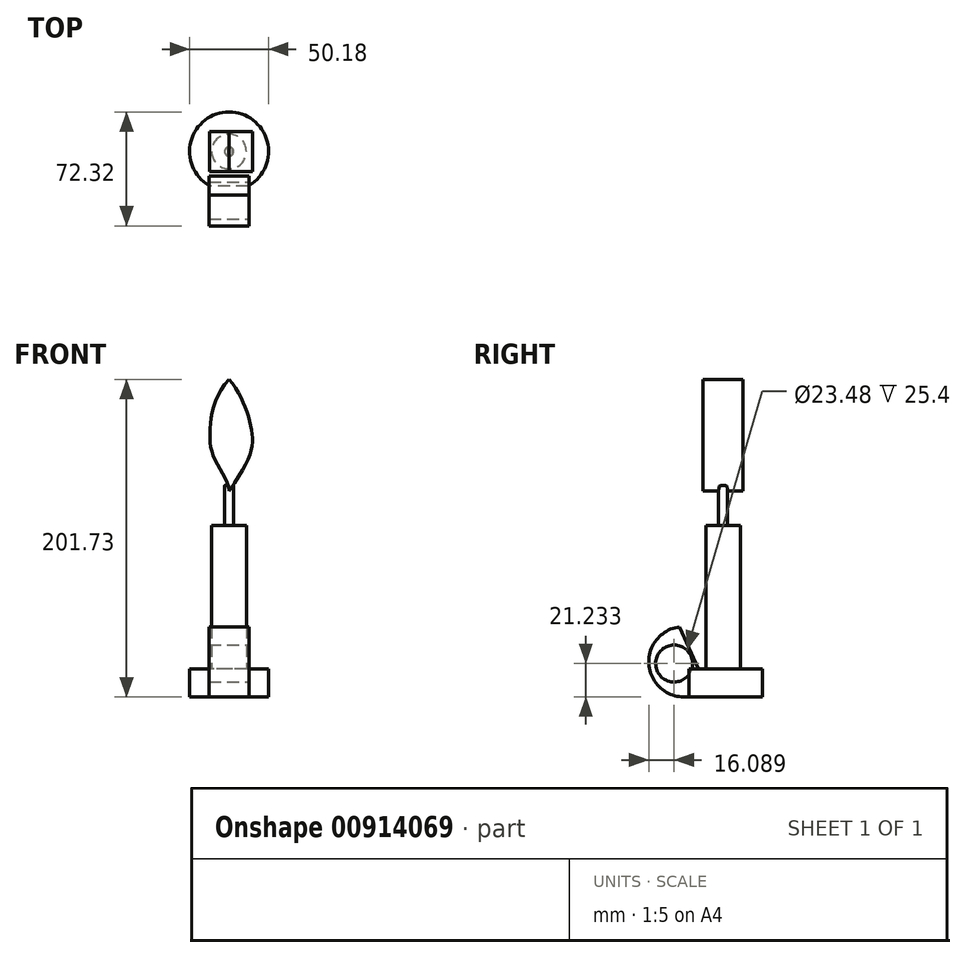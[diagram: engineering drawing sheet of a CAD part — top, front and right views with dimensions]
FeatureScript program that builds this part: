
annotation { "Feature Type Name" : "Feature", "Feature Type Description" : "" }
export const myFeature = defineFeature(function(context is Context, id is Id, definition is map)
    precondition{}
    {
        {
            var Q0;
            Q0=qCreatedBy(makeId("Top.planeOp"),FACE);
            var sketch = newSketch(context, id + "F0", { "sketchPlane" : qUnion([Q0])});
            skCircle(sketch, "E0", {"center": v(0, 0) * mm, "radius": 25.09 * mm});
            skCircle(sketch, "E1", {"center": v(0, 0) * mm, "radius": 9.92 * mm});
            skSolve(sketch);
        }
        {
            var Q0;
            Q0=makeQuery(id+"F0.imprint","IMPRINT",FACE,{"disambiguationData":[TD([[makeQuery(id+"F0.imprint","IMPRINT",EDGE,{"derivedFrom":sQuery(id+"F0.wireOp",EDGE,"E0")}),1.0]])]});
            extrude(context, id + "F1", {"entities" : qUnion([Q0]), "depth" : 17.53 * mm, "offsetDistance" : 25.4 * mm});
        }
        {
            var Q0;
            Q0=qCreatedBy(makeId("Top.planeOp"),FACE);
            var sketch = newSketch(context, id + "F2", { "sketchPlane" : qUnion([Q0])});
            skCircle(sketch, "E2", {"center": v(0, 0) * mm, "radius": 11.02 * mm});
            skSolve(sketch);
        }
        {
            var Q0;
            Q0=makeQuery(id+"F2.imprint","IMPRINT",FACE,{"disambiguationData":[TD([[makeQuery(id+"F2.imprint","IMPRINT",EDGE,{"derivedFrom":sQuery(id+"F2.wireOp",EDGE,"E2")}),1.0]])]});
            extrude(context, id + "F3", {"entities" : qUnion([Q0]), "operationType" : NewBodyOperationType.ADD, "depth" : 108.7 * mm, "offsetDistance" : 25.4 * mm});
        }
        {
            var Q0;
            Q0=makeQuery(id+"F3.opExtrude","CAP_FACE",FACE,{"disambiguationData":[OSD([sQuery(id+"F2.wireOp",EDGE,"E2")])],"isStart":false});
            cPlane(context, id + "F4", {"entities" : qUnion([Q0]), "cplaneType" : CPlaneType.OFFSET, "offset" : 25.4 * mm, "width" : 152.4 * mm, "height" : 152.4 * mm});
        }
        {
            var Q0;
            Q0=qCreatedBy(id+"F4.planeOp",FACE);
            var sketch = newSketch(context, id + "F5", { "sketchPlane" : qUnion([Q0])});
            skCircle(sketch, "E3", {"center": v(0, 0) * mm, "radius": 2.87 * mm});
            skSolve(sketch);
        }
        {
            var Q0;
            Q0=makeQuery(id+"F5.imprint","IMPRINT",FACE,{"disambiguationData":[TD([[makeQuery(id+"F5.imprint","IMPRINT",EDGE,{"derivedFrom":sQuery(id+"F5.wireOp",EDGE,"E3")}),1.0]])]});
            extrude(context, id + "F6", {"entities" : qUnion([Q0]), "operationType" : NewBodyOperationType.ADD, "oppositeDirection" : true, "depth" : 25.4 * mm, "offsetDistance" : 25.4 * mm});
        }
        {
            var Q0;
            Q0=qCreatedBy(makeId("Right.planeOp"),FACE);
            var sketch = newSketch(context, id + "F7", { "sketchPlane" : qUnion([Q0])});
            skArc(sketch, "E4", {"start": v(-27.61, 44.34) * mm, "mid": v(-47.05, 19.36) * mm, "end": v(-22.01, 0) * mm});
            skLineSegment(sketch, "E5", {"start": v(-27.61, 44.34) * mm, "end": v(-14, 13.6) * mm});
            skLineSegment(sketch, "E6", {"start": v(-14, 13.6) * mm, "end": v(-22.01, 0) * mm});
            skSolve(sketch);
        }
        {
            var Q0;
            Q0=makeQuery(id+"F7.imprint","IMPRINT",FACE,{"disambiguationData":[TD([[makeQuery(id+"F7.imprint","IMPRINT",EDGE,{"derivedFrom":sQuery(id+"F7.wireOp",EDGE,"E4")}),1.0]])]});
            extrude(context, id + "F8", {"entities" : qUnion([Q0]), "operationType" : NewBodyOperationType.ADD, "depth" : 25.4 * mm, "offsetDistance" : 25.4 * mm, "symmetric" : true});
        }
        {
            var Q0;
            Q0=qCreatedBy(makeId("Right.planeOp"),FACE);
            var sketch = newSketch(context, id + "F9", { "sketchPlane" : qUnion([Q0])});
            skCircle(sketch, "E7", {"center": v(-31.14, 21.04) * mm, "radius": 11.74 * mm});
            skSolve(sketch);
        }
        {
            var Q0;
            Q0=makeQuery(id+"F9.imprint","IMPRINT",FACE,{"disambiguationData":[TD([[makeQuery(id+"F9.imprint","IMPRINT",EDGE,{"derivedFrom":sQuery(id+"F9.wireOp",EDGE,"E7")}),1.0]])]});
            extrude(context, id + "F10", {"entities" : qUnion([Q0]), "operationType" : NewBodyOperationType.REMOVE, "oppositeDirection" : true, "depth" : 25.4 * mm, "offsetDistance" : 25.4 * mm, "symmetric" : true});
        }
        {
            var Q0;
            Q0=qCreatedBy(makeId("Front.planeOp"),FACE);
            var sketch = newSketch(context, id + "F11", { "sketchPlane" : qUnion([Q0])});
            skFitSpline(sketch, "E8", {"points": [v(0, 201.54) * mm, v(14.33, 169.29) * mm, v(0, 130.81) * mm], "startDerivative": vector(51.18, -62) * mm, "endDerivative": vector(-82.87, -116.52) * mm});
            skFitSpline(sketch, "E9", {"points": [v(0, 201.54) * mm, v(-12.04, 170.75) * mm, v(-9.13, 151) * mm, v(0, 130.81) * mm], "startDerivative": vector(-71.02, -74.2) * mm, "endDerivative": vector(0, -59.24) * mm});
            skSolve(sketch);
        }
        {
            var Q0;
            Q0 = qSketchRegion(id + "F11", true);
            extrude(context, id + "F12", {"entities" : qUnion([Q0]), "operationType" : NewBodyOperationType.ADD, "depth" : 25.4 * mm, "offsetDistance" : 25.4 * mm, "symmetric" : true});
        }
    });
